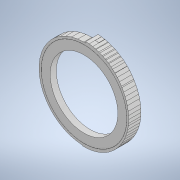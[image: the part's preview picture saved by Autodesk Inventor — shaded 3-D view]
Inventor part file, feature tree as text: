
AUTODESK INVENTOR PART (.ipt)
format: ipt  version: 2021 (Build 250183000, 183)  size: 427,520 bytes
history: native  units: mm
features: reference x133, extrude x3, other x3, sketch x2, plane x1
ambient origin geometry x8: Origin, YZ Plane, XZ Plane, XY Plane, X Axis, Y Axis, Z Axis, Center Point
bodies: Body1 (feature_tree)
feature tree (142):
  plane  "Work Plane1"
  sketch  "Sketch1"  dims[d4=3.0mm d5=0.0mm d6=1.0mm d7=0.0mm]
  extrude  "Extrusion3"  Depth=3.0mm TaperAngle=0.0deg
  extrude  "Extrusion4"  Depth=3.0mm
  extrude  "Extrusion5"  Depth=3.0mm
  reference  "Reference1"
  reference  "Reference2"
  reference  "Reference3"
  reference  "Reference8"
  reference  "Reference9"
  reference  "Reference10"
  reference  "Reference11"
  reference  "Reference12"
  reference  "Reference13"
  reference  "Reference14"
  reference  "Reference15"
  reference  "Reference16"
  reference  "Reference17"
  reference  "Reference18"
  reference  "Reference19"
  reference  "Reference20"
  reference  "Reference21"
  reference  "Reference22"
  reference  "Reference23"
  reference  "Reference24"
  reference  "Reference25"
  reference  "Reference26"
  reference  "Reference27"
  reference  "Reference28"
  reference  "Reference29"
  reference  "Reference30"
  reference  "Reference31"
  reference  "Reference32"
  reference  "Reference33"
  reference  "Reference34"
  reference  "Reference35"
  reference  "Reference36"
  reference  "Reference37"
  reference  "Reference38"
  reference  "Reference39"
  reference  "Reference40"
  reference  "Reference41"
  reference  "Reference42"
  reference  "Reference43"
  reference  "Reference44"
  reference  "Reference45"
  reference  "Reference46"
  reference  "Reference47"
  reference  "Reference48"
  reference  "Reference49"
  reference  "Reference50"
  reference  "Reference51"
  reference  "Reference52"
  reference  "Reference53"
  reference  "Reference54"
  reference  "Reference55"
  reference  "Reference56"
  reference  "Reference57"
  reference  "Reference58"
  reference  "Reference59"
  reference  "Reference60"
  reference  "Reference61"
  reference  "Reference62"
  reference  "Reference63"
  reference  "Reference64"
  reference  "Reference65"
  reference  "Reference66"
  reference  "Reference67"
  reference  "Reference68"
  reference  "Reference69"
  reference  "Reference70"
  reference  "Reference71"
  reference  "Reference72"
  reference  "Reference73"
  reference  "Reference74"
  reference  "Reference75"
  reference  "Reference76"
  reference  "Reference77"
  reference  "Reference78"
  reference  "Reference79"
  reference  "Reference80"
  reference  "Reference81"
  reference  "Reference82"
  reference  "Reference83"
  reference  "Reference84"
  reference  "Reference85"
  reference  "Reference86"
  reference  "Reference87"
  reference  "Reference89"
  reference  "Reference90"
  reference  "Reference91"
  reference  "Reference92"
  reference  "Reference93"
  reference  "Reference94"
  reference  "Reference95"
  reference  "Reference96"
  reference  "Reference97"
  reference  "Reference98"
  reference  "Reference99"
  reference  "Reference100"
  reference  "Reference101"
  reference  "Reference102"
  reference  "Reference103"
  reference  "Reference104"
  reference  "Reference105"
  reference  "Reference106"
  reference  "Reference107"
  reference  "Reference108"
  reference  "Reference109"
  reference  "Reference110"
  reference  "Reference111"
  reference  "Reference112"
  reference  "Reference113"
  reference  "Reference114"
  reference  "Reference115"
  reference  "Reference116"
  reference  "Reference117"
  reference  "Reference118"
  reference  "Reference119"
  reference  "Reference120"
  reference  "Reference121"
  reference  "Reference122"
  reference  "Reference123"
  reference  "Reference124"
  reference  "Reference125"
  reference  "Reference126"
  reference  "Reference127"
  reference  "Reference128"
  reference  "Reference129"
  reference  "Reference130"
  reference  "Reference131"
  reference  "Reference132"
  reference  "Reference133"
  reference  "Reference134"
  reference  "Reference135"
  reference  "Reference136"
  reference  "Reference137"
  reference  "Reference138"
  sketch  "Sketch3"  dims[d8=3.0mm d9=0.0mm d2=0.5mm d3=0.872665mm]
  other  "Z:\softHandProsthesis.iam"
  other  "softHandProsthesis.iam"
  other  "Righ_Hand_Palm:1"
